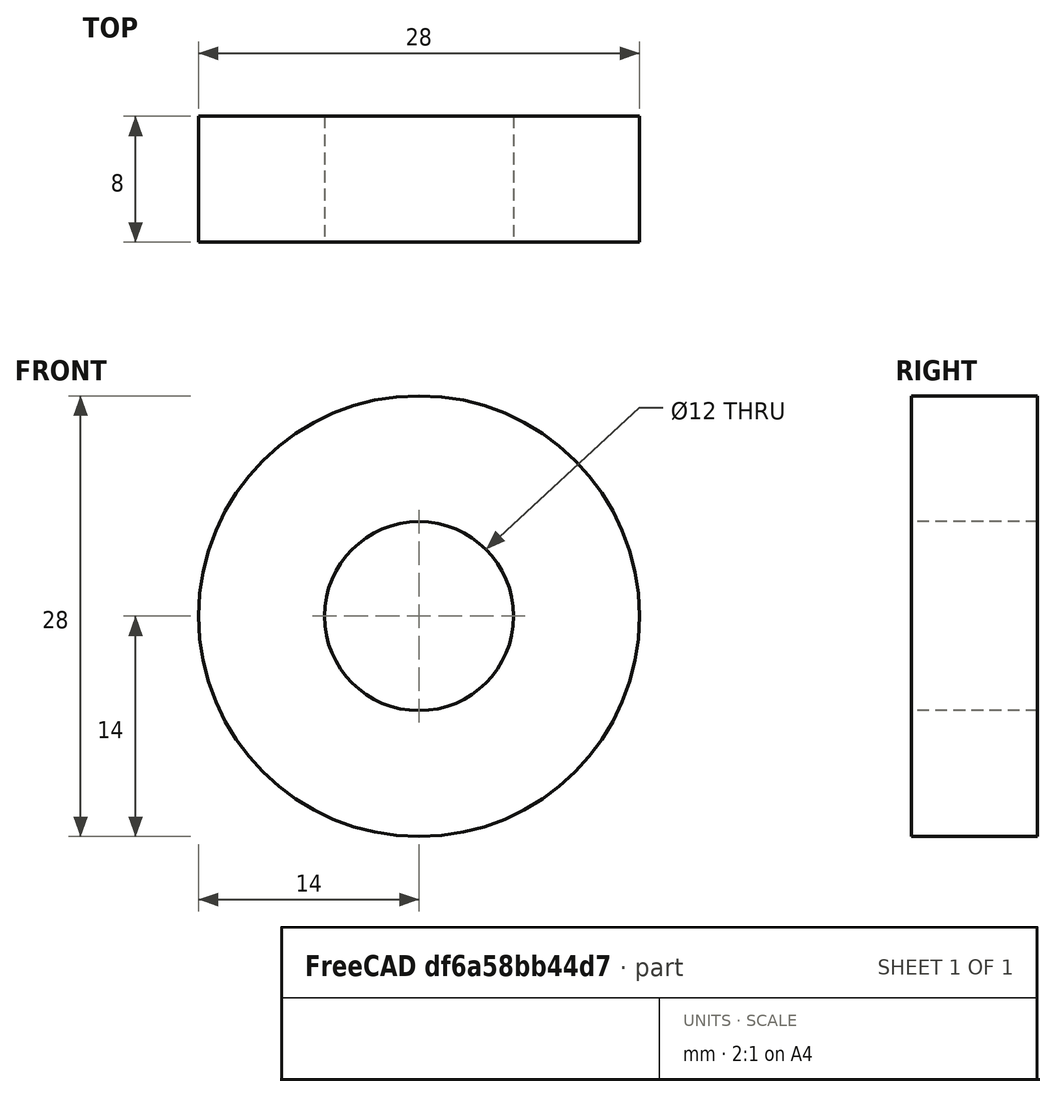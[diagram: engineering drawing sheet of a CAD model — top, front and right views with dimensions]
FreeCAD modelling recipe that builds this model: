
FCSTD DOCUMENT  (FreeCAD 0.21R33668 +7 (Git))
Label: 6001
License: All rights reserved
LicenseURL: https://en.wikipedia.org/wiki/All_rights_reserved
objects: Sketcher::SketchObject×1, PartDesign::Revolution×1, PartDesign::Body×1
note: 4 computed .brp shape members not serialized (recipe doc carries the construction recipe); baked Part::Feature solids carry a one-line shape summary decoded from their .brp

FEATURE [Sketcher::SketchObject] Sketch
  FullyConstrained = true
  MapMode = 5
  Placement = pos=(0,0,0) rot=(0.57735,0.57735,0.57735;2.0944rad)
  Support = -> [YZ_Plane]
  sketch-geometry (4):
    g0: LineSegment StartX=-4 StartY=14 StartZ=0 EndX=4 EndY=14 EndZ=0
    g1: LineSegment StartX=4 StartY=14 StartZ=0 EndX=4 EndY=6 EndZ=0
    g2: LineSegment StartX=4 StartY=6 StartZ=0 EndX=-4 EndY=6 EndZ=0
    g3: LineSegment StartX=-4 StartY=6 StartZ=0 EndX=-4 EndY=14 EndZ=0
  constraints (11):
    c: Coincident(g0,g1)
    c: Coincident(g1,g2)
    c: Coincident(g2,g3)
    c: Coincident(g3,g0)
    c: Horizontal(g2)
    c: Vertical(g1)
    c: Vertical(g3)
    c: DistanceY(g-1,g2) = 6
    c: DistanceY(g-1,g0) = 14
    c: DistanceX(g0,g0) = 8
    c: Symmetric(g0,g0,g-2)
FEATURE [PartDesign::Revolution] Revolution
  Angle = 360
  Axis = (3e-16,1,-2e-16)
  Base = (0,0,0)
  Placement = pos=(0,0,0) rot=(1,1,1;2.0944rad)
  Profile = -> Sketch
  ReferenceAxis = -> Sketch [H_Axis]
FEATURE [PartDesign::Body] Body  label="6001"
  Group = -> [Sketch,Revolution]
  Origin = -> Origin
  Tip = -> Revolution
